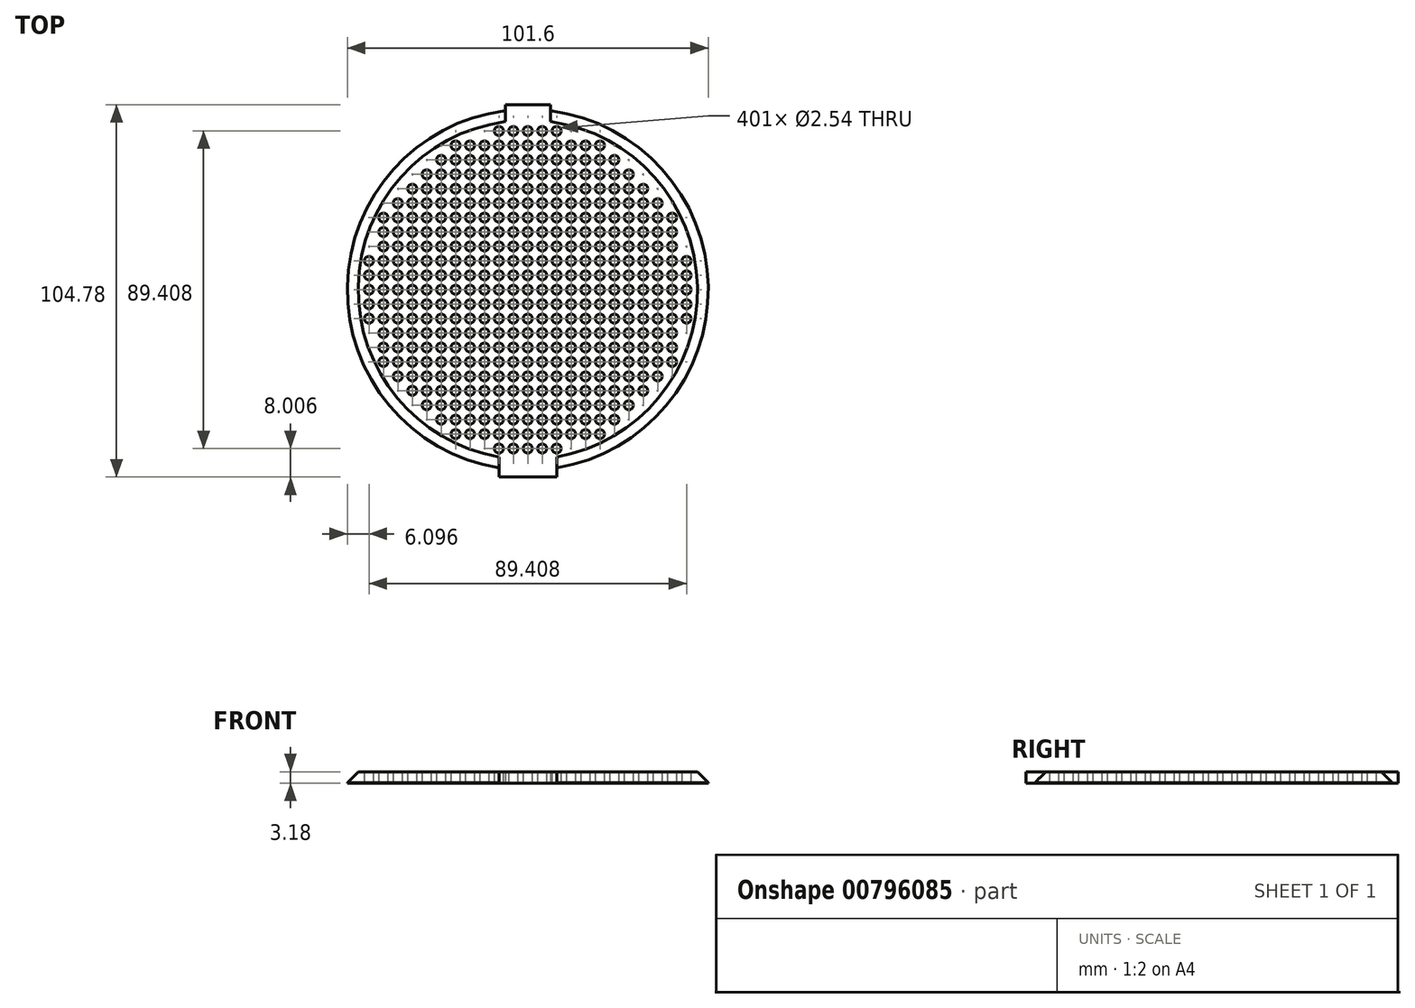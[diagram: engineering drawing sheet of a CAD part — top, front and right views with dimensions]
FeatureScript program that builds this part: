
annotation { "Feature Type Name" : "Feature", "Feature Type Description" : "" }
export const myFeature = defineFeature(function(context is Context, id is Id, definition is map)
    precondition{}
    {
        {
            var Q0;
            Q0=qCreatedBy(makeId("Top.planeOp"),FACE);
            var sketch = newSketch(context, id + "F0", { "sketchPlane" : qUnion([Q0])});
            skCircle(sketch, "E0", {"center": v(0, 0) * mm, "radius": 50.8 * mm});
            skSolve(sketch);
        }
        {
            var Q0;
            Q0 = qSketchRegion(id + "F0", true);
            extrude(context, id + "F1", {"entities" : qUnion([Q0]), "depth" : 3.17 * mm, "offsetDistance" : 25.4 * mm});
        }
        {
            var Q0;
            Q0=makeQuery(id+"F1.opExtrude","CAP_EDGE",EDGE,{"disambiguationData":[OSD([sQuery(id+"F0.wireOp",EDGE,"E0")])],"isStart":false});
            chamfer(context, id + "F2", {"entities" : qUnion([Q0]), "width" : 3.05 * mm, "tangentPropagation" : true});
        }
        {
            var Q0;
            Q0=makeQuery(id+"F1.opExtrude","CAP_FACE",FACE,{"disambiguationData":[OSD([sQuery(id+"F0.wireOp",EDGE,"E0")])],"isStart":false});
            var sketch = newSketch(context, id + "F3", { "sketchPlane" : qUnion([Q0])});
            skCircle(sketch, "E1", {"center": v(0, 0) * mm, "radius": 1.27 * mm});
            skCircle(sketch, "E2.0.1.0", {"center": v(0, 4.06) * mm, "radius": 1.27 * mm});
            skCircle(sketch, "E2.0.2.0", {"center": v(0, 8.13) * mm, "radius": 1.27 * mm});
            skCircle(sketch, "E2.0.3.0", {"center": v(0, 12.2) * mm, "radius": 1.27 * mm});
            skCircle(sketch, "E2.0.4.0", {"center": v(0, 16.26) * mm, "radius": 1.27 * mm});
            skCircle(sketch, "E2.0.5.0", {"center": v(0, 20.32) * mm, "radius": 1.27 * mm});
            skCircle(sketch, "E2.0.6.0", {"center": v(0, 24.38) * mm, "radius": 1.27 * mm});
            skCircle(sketch, "E2.0.7.0", {"center": v(0, 28.45) * mm, "radius": 1.27 * mm});
            skCircle(sketch, "E2.0.8.0", {"center": v(0, 32.51) * mm, "radius": 1.27 * mm});
            skCircle(sketch, "E2.0.9.0", {"center": v(0, 36.58) * mm, "radius": 1.27 * mm});
            skCircle(sketch, "E2.0.10.0", {"center": v(0, 40.64) * mm, "radius": 1.27 * mm});
            skCircle(sketch, "E2.0.11.0", {"center": v(0, 44.7) * mm, "radius": 1.27 * mm});
            skCircle(sketch, "E2.1.0.0", {"center": v(4.06, 0) * mm, "radius": 1.27 * mm});
            skCircle(sketch, "E2.1.1.0", {"center": v(4.06, 4.06) * mm, "radius": 1.27 * mm});
            skCircle(sketch, "E2.1.2.0", {"center": v(4.06, 8.13) * mm, "radius": 1.27 * mm});
            skCircle(sketch, "E2.1.3.0", {"center": v(4.06, 12.2) * mm, "radius": 1.27 * mm});
            skCircle(sketch, "E2.1.4.0", {"center": v(4.06, 16.26) * mm, "radius": 1.27 * mm});
            skCircle(sketch, "E2.1.5.0", {"center": v(4.06, 20.32) * mm, "radius": 1.27 * mm});
            skCircle(sketch, "E2.1.6.0", {"center": v(4.06, 24.38) * mm, "radius": 1.27 * mm});
            skCircle(sketch, "E2.1.7.0", {"center": v(4.06, 28.45) * mm, "radius": 1.27 * mm});
            skCircle(sketch, "E2.1.8.0", {"center": v(4.06, 32.51) * mm, "radius": 1.27 * mm});
            skCircle(sketch, "E2.1.9.0", {"center": v(4.06, 36.58) * mm, "radius": 1.27 * mm});
            skCircle(sketch, "E2.1.10.0", {"center": v(4.06, 40.64) * mm, "radius": 1.27 * mm});
            skCircle(sketch, "E2.1.11.0", {"center": v(4.06, 44.7) * mm, "radius": 1.27 * mm});
            skCircle(sketch, "E2.2.0.0", {"center": v(8.13, 0) * mm, "radius": 1.27 * mm});
            skCircle(sketch, "E2.2.1.0", {"center": v(8.13, 4.06) * mm, "radius": 1.27 * mm});
            skCircle(sketch, "E2.2.2.0", {"center": v(8.13, 8.13) * mm, "radius": 1.27 * mm});
            skCircle(sketch, "E2.2.3.0", {"center": v(8.13, 12.2) * mm, "radius": 1.27 * mm});
            skCircle(sketch, "E2.2.4.0", {"center": v(8.13, 16.26) * mm, "radius": 1.27 * mm});
            skCircle(sketch, "E2.2.5.0", {"center": v(8.13, 20.32) * mm, "radius": 1.27 * mm});
            skCircle(sketch, "E2.2.6.0", {"center": v(8.13, 24.38) * mm, "radius": 1.27 * mm});
            skCircle(sketch, "E2.2.7.0", {"center": v(8.13, 28.45) * mm, "radius": 1.27 * mm});
            skCircle(sketch, "E2.2.8.0", {"center": v(8.13, 32.51) * mm, "radius": 1.27 * mm});
            skCircle(sketch, "E2.2.9.0", {"center": v(8.13, 36.58) * mm, "radius": 1.27 * mm});
            skCircle(sketch, "E2.2.10.0", {"center": v(8.13, 40.64) * mm, "radius": 1.27 * mm});
            skCircle(sketch, "E2.2.11.0", {"center": v(8.13, 44.7) * mm, "radius": 1.27 * mm});
            skCircle(sketch, "E2.3.0.0", {"center": v(12.2, 0) * mm, "radius": 1.27 * mm});
            skCircle(sketch, "E2.3.1.0", {"center": v(12.2, 4.06) * mm, "radius": 1.27 * mm});
            skCircle(sketch, "E2.3.2.0", {"center": v(12.2, 8.13) * mm, "radius": 1.27 * mm});
            skCircle(sketch, "E2.3.3.0", {"center": v(12.2, 12.2) * mm, "radius": 1.27 * mm});
            skCircle(sketch, "E2.3.4.0", {"center": v(12.2, 16.26) * mm, "radius": 1.27 * mm});
            skCircle(sketch, "E2.3.5.0", {"center": v(12.2, 20.32) * mm, "radius": 1.27 * mm});
            skCircle(sketch, "E2.3.6.0", {"center": v(12.2, 24.38) * mm, "radius": 1.27 * mm});
            skCircle(sketch, "E2.3.7.0", {"center": v(12.2, 28.45) * mm, "radius": 1.27 * mm});
            skCircle(sketch, "E2.3.8.0", {"center": v(12.2, 32.51) * mm, "radius": 1.27 * mm});
            skCircle(sketch, "E2.3.9.0", {"center": v(12.2, 36.58) * mm, "radius": 1.27 * mm});
            skCircle(sketch, "E2.3.10.0", {"center": v(12.2, 40.64) * mm, "radius": 1.27 * mm});
            skCircle(sketch, "E2.4.0.0", {"center": v(16.26, 0) * mm, "radius": 1.27 * mm});
            skCircle(sketch, "E2.4.1.0", {"center": v(16.26, 4.06) * mm, "radius": 1.27 * mm});
            skCircle(sketch, "E2.4.2.0", {"center": v(16.26, 8.13) * mm, "radius": 1.27 * mm});
            skCircle(sketch, "E2.4.3.0", {"center": v(16.26, 12.2) * mm, "radius": 1.27 * mm});
            skCircle(sketch, "E2.4.4.0", {"center": v(16.26, 16.26) * mm, "radius": 1.27 * mm});
            skCircle(sketch, "E2.4.5.0", {"center": v(16.26, 20.32) * mm, "radius": 1.27 * mm});
            skCircle(sketch, "E2.4.6.0", {"center": v(16.26, 24.38) * mm, "radius": 1.27 * mm});
            skCircle(sketch, "E2.4.7.0", {"center": v(16.26, 28.45) * mm, "radius": 1.27 * mm});
            skCircle(sketch, "E2.4.8.0", {"center": v(16.26, 32.51) * mm, "radius": 1.27 * mm});
            skCircle(sketch, "E2.4.9.0", {"center": v(16.26, 36.58) * mm, "radius": 1.27 * mm});
            skCircle(sketch, "E2.4.10.0", {"center": v(16.26, 40.64) * mm, "radius": 1.27 * mm});
            skCircle(sketch, "E2.5.0.0", {"center": v(20.32, 0) * mm, "radius": 1.27 * mm});
            skCircle(sketch, "E2.5.1.0", {"center": v(20.32, 4.06) * mm, "radius": 1.27 * mm});
            skCircle(sketch, "E2.5.2.0", {"center": v(20.32, 8.13) * mm, "radius": 1.27 * mm});
            skCircle(sketch, "E2.5.3.0", {"center": v(20.32, 12.2) * mm, "radius": 1.27 * mm});
            skCircle(sketch, "E2.5.4.0", {"center": v(20.32, 16.26) * mm, "radius": 1.27 * mm});
            skCircle(sketch, "E2.5.5.0", {"center": v(20.32, 20.32) * mm, "radius": 1.27 * mm});
            skCircle(sketch, "E2.5.6.0", {"center": v(20.32, 24.38) * mm, "radius": 1.27 * mm});
            skCircle(sketch, "E2.5.7.0", {"center": v(20.32, 28.45) * mm, "radius": 1.27 * mm});
            skCircle(sketch, "E2.5.8.0", {"center": v(20.32, 32.51) * mm, "radius": 1.27 * mm});
            skCircle(sketch, "E2.5.9.0", {"center": v(20.32, 36.58) * mm, "radius": 1.27 * mm});
            skCircle(sketch, "E2.5.10.0", {"center": v(20.32, 40.64) * mm, "radius": 1.27 * mm});
            skCircle(sketch, "E2.6.0.0", {"center": v(24.38, 0) * mm, "radius": 1.27 * mm});
            skCircle(sketch, "E2.6.1.0", {"center": v(24.38, 4.06) * mm, "radius": 1.27 * mm});
            skCircle(sketch, "E2.6.2.0", {"center": v(24.38, 8.13) * mm, "radius": 1.27 * mm});
            skCircle(sketch, "E2.6.3.0", {"center": v(24.38, 12.2) * mm, "radius": 1.27 * mm});
            skCircle(sketch, "E2.6.4.0", {"center": v(24.38, 16.26) * mm, "radius": 1.27 * mm});
            skCircle(sketch, "E2.6.5.0", {"center": v(24.38, 20.32) * mm, "radius": 1.27 * mm});
            skCircle(sketch, "E2.6.6.0", {"center": v(24.38, 24.38) * mm, "radius": 1.27 * mm});
            skCircle(sketch, "E2.6.7.0", {"center": v(24.38, 28.45) * mm, "radius": 1.27 * mm});
            skCircle(sketch, "E2.6.8.0", {"center": v(24.38, 32.51) * mm, "radius": 1.27 * mm});
            skCircle(sketch, "E2.6.9.0", {"center": v(24.38, 36.58) * mm, "radius": 1.27 * mm});
            skCircle(sketch, "E2.7.0.0", {"center": v(28.45, 0) * mm, "radius": 1.27 * mm});
            skCircle(sketch, "E2.7.1.0", {"center": v(28.45, 4.06) * mm, "radius": 1.27 * mm});
            skCircle(sketch, "E2.7.2.0", {"center": v(28.45, 8.13) * mm, "radius": 1.27 * mm});
            skCircle(sketch, "E2.7.3.0", {"center": v(28.45, 12.2) * mm, "radius": 1.27 * mm});
            skCircle(sketch, "E2.7.4.0", {"center": v(28.45, 16.26) * mm, "radius": 1.27 * mm});
            skCircle(sketch, "E2.7.5.0", {"center": v(28.45, 20.32) * mm, "radius": 1.27 * mm});
            skCircle(sketch, "E2.7.6.0", {"center": v(28.45, 24.38) * mm, "radius": 1.27 * mm});
            skCircle(sketch, "E2.7.7.0", {"center": v(28.45, 28.45) * mm, "radius": 1.27 * mm});
            skCircle(sketch, "E2.7.8.0", {"center": v(28.45, 32.51) * mm, "radius": 1.27 * mm});
            skCircle(sketch, "E2.8.0.0", {"center": v(32.51, 0) * mm, "radius": 1.27 * mm});
            skCircle(sketch, "E2.8.1.0", {"center": v(32.51, 4.06) * mm, "radius": 1.27 * mm});
            skCircle(sketch, "E2.8.2.0", {"center": v(32.51, 8.13) * mm, "radius": 1.27 * mm});
            skCircle(sketch, "E2.8.3.0", {"center": v(32.51, 12.2) * mm, "radius": 1.27 * mm});
            skCircle(sketch, "E2.8.4.0", {"center": v(32.51, 16.26) * mm, "radius": 1.27 * mm});
            skCircle(sketch, "E2.8.5.0", {"center": v(32.51, 20.32) * mm, "radius": 1.27 * mm});
            skCircle(sketch, "E2.8.6.0", {"center": v(32.51, 24.38) * mm, "radius": 1.27 * mm});
            skCircle(sketch, "E2.8.7.0", {"center": v(32.51, 28.45) * mm, "radius": 1.27 * mm});
            skCircle(sketch, "E2.9.0.0", {"center": v(36.58, 0) * mm, "radius": 1.27 * mm});
            skCircle(sketch, "E2.9.1.0", {"center": v(36.58, 4.06) * mm, "radius": 1.27 * mm});
            skCircle(sketch, "E2.9.2.0", {"center": v(36.58, 8.13) * mm, "radius": 1.27 * mm});
            skCircle(sketch, "E2.9.3.0", {"center": v(36.58, 12.2) * mm, "radius": 1.27 * mm});
            skCircle(sketch, "E2.9.4.0", {"center": v(36.58, 16.26) * mm, "radius": 1.27 * mm});
            skCircle(sketch, "E2.9.5.0", {"center": v(36.58, 20.32) * mm, "radius": 1.27 * mm});
            skCircle(sketch, "E2.9.6.0", {"center": v(36.58, 24.38) * mm, "radius": 1.27 * mm});
            skCircle(sketch, "E2.10.0.0", {"center": v(40.64, 0) * mm, "radius": 1.27 * mm});
            skCircle(sketch, "E2.10.1.0", {"center": v(40.64, 4.06) * mm, "radius": 1.27 * mm});
            skCircle(sketch, "E2.10.2.0", {"center": v(40.64, 8.13) * mm, "radius": 1.27 * mm});
            skCircle(sketch, "E2.10.3.0", {"center": v(40.64, 12.2) * mm, "radius": 1.27 * mm});
            skCircle(sketch, "E2.10.4.0", {"center": v(40.64, 16.26) * mm, "radius": 1.27 * mm});
            skCircle(sketch, "E2.10.5.0", {"center": v(40.64, 20.32) * mm, "radius": 1.27 * mm});
            skCircle(sketch, "E2.11.0.0", {"center": v(44.7, 0) * mm, "radius": 1.27 * mm});
            skCircle(sketch, "E2.11.1.0", {"center": v(44.7, 4.06) * mm, "radius": 1.27 * mm});
            skCircle(sketch, "E2.11.2.0", {"center": v(44.7, 8.13) * mm, "radius": 1.27 * mm});
            skLineSegment(sketch, "E2.direction1", {"start": v(0, 0) * mm, "end": v(4.06, 0) * mm, "construction": true});
            skLineSegment(sketch, "E2.direction2", {"start": v(0, 0) * mm, "end": v(0, 4.06) * mm, "construction": true});
            skCircle(sketch, "E3.MirrorC", {"center": v(-4.06, 4.06) * mm, "radius": 1.27 * mm});
            skCircle(sketch, "E4.MirrorC", {"center": v(-28.45, 0) * mm, "radius": 1.27 * mm});
            skCircle(sketch, "E5.MirrorC", {"center": v(-8.13, 20.32) * mm, "radius": 1.27 * mm});
            skCircle(sketch, "E6.MirrorC", {"center": v(-16.26, 20.32) * mm, "radius": 1.27 * mm});
            skCircle(sketch, "E7.MirrorC", {"center": v(-32.51, 24.38) * mm, "radius": 1.27 * mm});
            skCircle(sketch, "E8.MirrorC", {"center": v(-44.7, 4.06) * mm, "radius": 1.27 * mm});
            skCircle(sketch, "E9.MirrorC", {"center": v(-12.2, 36.58) * mm, "radius": 1.27 * mm});
            skCircle(sketch, "E10.MirrorC", {"center": v(-12.2, 40.64) * mm, "radius": 1.27 * mm});
            skCircle(sketch, "E11.MirrorC", {"center": v(-24.38, 0) * mm, "radius": 1.27 * mm});
            skCircle(sketch, "E12.MirrorC", {"center": v(-20.32, 12.2) * mm, "radius": 1.27 * mm});
            skCircle(sketch, "E13.MirrorC", {"center": v(-28.45, 20.32) * mm, "radius": 1.27 * mm});
            skCircle(sketch, "E14.MirrorC", {"center": v(-24.38, 32.51) * mm, "radius": 1.27 * mm});
            skCircle(sketch, "E15.MirrorC", {"center": v(-4.06, 36.58) * mm, "radius": 1.27 * mm});
            skCircle(sketch, "E16.MirrorC", {"center": v(-40.64, 20.32) * mm, "radius": 1.27 * mm});
            skCircle(sketch, "E17.MirrorC", {"center": v(-24.38, 28.45) * mm, "radius": 1.27 * mm});
            skCircle(sketch, "E18.MirrorC", {"center": v(-8.13, 16.26) * mm, "radius": 1.27 * mm});
            skCircle(sketch, "E19.MirrorC", {"center": v(-32.51, 16.26) * mm, "radius": 1.27 * mm});
            skCircle(sketch, "E20.MirrorC", {"center": v(-20.32, 8.13) * mm, "radius": 1.27 * mm});
            skCircle(sketch, "E21.MirrorC", {"center": v(-32.51, 12.2) * mm, "radius": 1.27 * mm});
            skCircle(sketch, "E22.MirrorC", {"center": v(-24.38, 24.38) * mm, "radius": 1.27 * mm});
            skCircle(sketch, "E23.MirrorC", {"center": v(-44.7, 0) * mm, "radius": 1.27 * mm});
            skCircle(sketch, "E24.MirrorC", {"center": v(-12.2, 0) * mm, "radius": 1.27 * mm});
            skCircle(sketch, "E25.MirrorC", {"center": v(-20.32, 40.64) * mm, "radius": 1.27 * mm});
            skCircle(sketch, "E26.MirrorC", {"center": v(-4.06, 32.51) * mm, "radius": 1.27 * mm});
            skCircle(sketch, "E27.MirrorC", {"center": v(-40.64, 16.26) * mm, "radius": 1.27 * mm});
            skCircle(sketch, "E28.MirrorC", {"center": v(-8.13, 12.2) * mm, "radius": 1.27 * mm});
            skCircle(sketch, "E29.MirrorC", {"center": v(-12.2, 28.45) * mm, "radius": 1.27 * mm});
            skCircle(sketch, "E30.MirrorC", {"center": v(-20.32, 4.06) * mm, "radius": 1.27 * mm});
            skCircle(sketch, "E31.MirrorC", {"center": v(-4.06, 28.45) * mm, "radius": 1.27 * mm});
            skCircle(sketch, "E32.MirrorC", {"center": v(-32.51, 8.13) * mm, "radius": 1.27 * mm});
            skCircle(sketch, "E33.MirrorC", {"center": v(-8.13, 8.13) * mm, "radius": 1.27 * mm});
            skCircle(sketch, "E34.MirrorC", {"center": v(-12.2, 24.38) * mm, "radius": 1.27 * mm});
            skCircle(sketch, "E35.MirrorC", {"center": v(-4.06, 0) * mm, "radius": 1.27 * mm});
            skCircle(sketch, "E36.MirrorC", {"center": v(-8.13, 40.64) * mm, "radius": 1.27 * mm});
            skCircle(sketch, "E37.MirrorC", {"center": v(-4.06, 24.38) * mm, "radius": 1.27 * mm});
            skCircle(sketch, "E38.MirrorC", {"center": v(-36.58, 12.2) * mm, "radius": 1.27 * mm});
            skCircle(sketch, "E39.MirrorC", {"center": v(-8.13, 4.06) * mm, "radius": 1.27 * mm});
            skCircle(sketch, "E40.MirrorC", {"center": v(-16.26, 40.64) * mm, "radius": 1.27 * mm});
            skCircle(sketch, "E41.MirrorC", {"center": v(-8.13, 44.7) * mm, "radius": 1.27 * mm});
            skCircle(sketch, "E42.MirrorC", {"center": v(-16.26, 16.26) * mm, "radius": 1.27 * mm});
            skCircle(sketch, "E43.MirrorC", {"center": v(-20.32, 36.58) * mm, "radius": 1.27 * mm});
            skCircle(sketch, "E44.MirrorC", {"center": v(-28.45, 16.26) * mm, "radius": 1.27 * mm});
            skCircle(sketch, "E45.MirrorC", {"center": v(-16.26, 8.13) * mm, "radius": 1.27 * mm});
            skCircle(sketch, "E46.MirrorC", {"center": v(-8.13, 36.58) * mm, "radius": 1.27 * mm});
            skCircle(sketch, "E47.MirrorC", {"center": v(-20.32, 28.45) * mm, "radius": 1.27 * mm});
            skCircle(sketch, "E48.MirrorC", {"center": v(-28.45, 8.13) * mm, "radius": 1.27 * mm});
            skCircle(sketch, "E49.MirrorC", {"center": v(-4.06, 20.32) * mm, "radius": 1.27 * mm});
            skCircle(sketch, "E50.MirrorC", {"center": v(-40.64, 4.06) * mm, "radius": 1.27 * mm});
            skCircle(sketch, "E51.MirrorC", {"center": v(-24.38, 12.2) * mm, "radius": 1.27 * mm});
            skCircle(sketch, "E52.MirrorC", {"center": v(-24.38, 20.32) * mm, "radius": 1.27 * mm});
            skCircle(sketch, "E53.MirrorC", {"center": v(-40.64, 12.2) * mm, "radius": 1.27 * mm});
            skCircle(sketch, "E54.MirrorC", {"center": v(-32.51, 0) * mm, "radius": 1.27 * mm});
            skCircle(sketch, "E55.MirrorC", {"center": v(-12.2, 16.26) * mm, "radius": 1.27 * mm});
            skCircle(sketch, "E56.MirrorC", {"center": v(-16.26, 36.58) * mm, "radius": 1.27 * mm});
            skCircle(sketch, "E57.MirrorC", {"center": v(-24.38, 8.13) * mm, "radius": 1.27 * mm});
            skCircle(sketch, "E58.MirrorC", {"center": v(-20.32, 0) * mm, "radius": 1.27 * mm});
            skCircle(sketch, "E59.MirrorC", {"center": v(-28.45, 32.51) * mm, "radius": 1.27 * mm});
            skCircle(sketch, "E60.MirrorC", {"center": v(-40.64, 0) * mm, "radius": 1.27 * mm});
            skCircle(sketch, "E61.MirrorC", {"center": v(-4.06, 16.26) * mm, "radius": 1.27 * mm});
            skCircle(sketch, "E62.MirrorC", {"center": v(-4.06, 44.7) * mm, "radius": 1.27 * mm});
            skCircle(sketch, "E63.MirrorC", {"center": v(-12.2, 12.2) * mm, "radius": 1.27 * mm});
            skCircle(sketch, "E64.MirrorC", {"center": v(-16.26, 32.51) * mm, "radius": 1.27 * mm});
            skCircle(sketch, "E65.MirrorC", {"center": v(-36.58, 0) * mm, "radius": 1.27 * mm});
            skLineSegment(sketch, "E66.MirrorCS", {"start": v(0, 0) * mm, "end": v(-4.06, 0) * mm, "construction": true});
            skCircle(sketch, "E67.MirrorC", {"center": v(-8.13, 32.51) * mm, "radius": 1.27 * mm});
            skCircle(sketch, "E68.MirrorC", {"center": v(-16.26, 4.06) * mm, "radius": 1.27 * mm});
            skCircle(sketch, "E69.MirrorC", {"center": v(-20.32, 24.38) * mm, "radius": 1.27 * mm});
            skCircle(sketch, "E70.MirrorC", {"center": v(-28.45, 4.06) * mm, "radius": 1.27 * mm});
            skCircle(sketch, "E71.MirrorC", {"center": v(-32.51, 28.45) * mm, "radius": 1.27 * mm});
            skCircle(sketch, "E72.MirrorC", {"center": v(-16.26, 0) * mm, "radius": 1.27 * mm});
            skCircle(sketch, "E73.MirrorC", {"center": v(-24.38, 4.06) * mm, "radius": 1.27 * mm});
            skCircle(sketch, "E74.MirrorC", {"center": v(-16.26, 28.45) * mm, "radius": 1.27 * mm});
            skCircle(sketch, "E75.MirrorC", {"center": v(-28.45, 28.45) * mm, "radius": 1.27 * mm});
            skCircle(sketch, "E76.MirrorC", {"center": v(-4.06, 40.64) * mm, "radius": 1.27 * mm});
            skCircle(sketch, "E77.MirrorC", {"center": v(-36.58, 20.32) * mm, "radius": 1.27 * mm});
            skCircle(sketch, "E78.MirrorC", {"center": v(-36.58, 8.13) * mm, "radius": 1.27 * mm});
            skCircle(sketch, "E79.MirrorC", {"center": v(-12.2, 4.06) * mm, "radius": 1.27 * mm});
            skCircle(sketch, "E80.MirrorC", {"center": v(-8.13, 24.38) * mm, "radius": 1.27 * mm});
            skCircle(sketch, "E81.MirrorC", {"center": v(-16.26, 24.38) * mm, "radius": 1.27 * mm});
            skCircle(sketch, "E82.MirrorC", {"center": v(-20.32, 16.26) * mm, "radius": 1.27 * mm});
            skCircle(sketch, "E83.MirrorC", {"center": v(-24.38, 36.58) * mm, "radius": 1.27 * mm});
            skCircle(sketch, "E84.MirrorC", {"center": v(-28.45, 24.38) * mm, "radius": 1.27 * mm});
            skCircle(sketch, "E85.MirrorC", {"center": v(-16.26, 12.2) * mm, "radius": 1.27 * mm});
            skCircle(sketch, "E86.MirrorC", {"center": v(-12.2, 32.51) * mm, "radius": 1.27 * mm});
            skCircle(sketch, "E87.MirrorC", {"center": v(-20.32, 32.51) * mm, "radius": 1.27 * mm});
            skCircle(sketch, "E88.MirrorC", {"center": v(-4.06, 12.2) * mm, "radius": 1.27 * mm});
            skCircle(sketch, "E89.MirrorC", {"center": v(-28.45, 12.2) * mm, "radius": 1.27 * mm});
            skCircle(sketch, "E90.MirrorC", {"center": v(-4.06, 8.13) * mm, "radius": 1.27 * mm});
            skCircle(sketch, "E91.MirrorC", {"center": v(-24.38, 16.26) * mm, "radius": 1.27 * mm});
            skCircle(sketch, "E92.MirrorC", {"center": v(-32.51, 4.06) * mm, "radius": 1.27 * mm});
            skCircle(sketch, "E93.MirrorC", {"center": v(-40.64, 8.13) * mm, "radius": 1.27 * mm});
            skCircle(sketch, "E94.MirrorC", {"center": v(-12.2, 20.32) * mm, "radius": 1.27 * mm});
            skCircle(sketch, "E95.MirrorC", {"center": v(-8.13, 0) * mm, "radius": 1.27 * mm});
            skCircle(sketch, "E96.MirrorC", {"center": v(-36.58, 4.06) * mm, "radius": 1.27 * mm});
            skCircle(sketch, "E97.MirrorC", {"center": v(-36.58, 24.38) * mm, "radius": 1.27 * mm});
            skCircle(sketch, "E98.MirrorC", {"center": v(-44.7, 8.13) * mm, "radius": 1.27 * mm});
            skCircle(sketch, "E99.MirrorC", {"center": v(-8.13, 28.45) * mm, "radius": 1.27 * mm});
            skCircle(sketch, "E100.MirrorC", {"center": v(-12.2, 8.13) * mm, "radius": 1.27 * mm});
            skCircle(sketch, "E101.MirrorC", {"center": v(-20.32, 20.32) * mm, "radius": 1.27 * mm});
            skCircle(sketch, "E102.MirrorC", {"center": v(-36.58, 16.26) * mm, "radius": 1.27 * mm});
            skCircle(sketch, "E103.MirrorC", {"center": v(-32.51, 20.32) * mm, "radius": 1.27 * mm});
            skCircle(sketch, "E104.MirrorC", {"center": v(0, -44.7) * mm, "radius": 1.27 * mm});
            skCircle(sketch, "E105.MirrorC", {"center": v(0, -40.64) * mm, "radius": 1.27 * mm});
            skCircle(sketch, "E106.MirrorC", {"center": v(0, -32.51) * mm, "radius": 1.27 * mm});
            skCircle(sketch, "E107.MirrorC", {"center": v(4.06, -4.06) * mm, "radius": 1.27 * mm});
            skCircle(sketch, "E108.MirrorC", {"center": v(0, -12.2) * mm, "radius": 1.27 * mm});
            skCircle(sketch, "E109.MirrorC", {"center": v(0, -36.58) * mm, "radius": 1.27 * mm});
            skCircle(sketch, "E110.MirrorC", {"center": v(0, -24.38) * mm, "radius": 1.27 * mm});
            skCircle(sketch, "E111.MirrorC", {"center": v(0, -28.45) * mm, "radius": 1.27 * mm});
            skCircle(sketch, "E112.MirrorC", {"center": v(0, -20.32) * mm, "radius": 1.27 * mm});
            skCircle(sketch, "E113.MirrorC", {"center": v(0, -8.13) * mm, "radius": 1.27 * mm});
            skCircle(sketch, "E114.MirrorC", {"center": v(0, -16.26) * mm, "radius": 1.27 * mm});
            skLineSegment(sketch, "E115.MirrorCS", {"start": v(0, 0) * mm, "end": v(0, -4.06) * mm, "construction": true});
            skCircle(sketch, "E116.MirrorC", {"center": v(0, -4.06) * mm, "radius": 1.27 * mm});
            skCircle(sketch, "E117.MirrorC", {"center": v(-8.13, -36.58) * mm, "radius": 1.27 * mm});
            skCircle(sketch, "E118.MirrorC", {"center": v(-24.38, -4.06) * mm, "radius": 1.27 * mm});
            skCircle(sketch, "E119.MirrorC", {"center": v(-4.06, -12.2) * mm, "radius": 1.27 * mm});
            skCircle(sketch, "E120.MirrorC", {"center": v(36.58, -16.26) * mm, "radius": 1.27 * mm});
            skCircle(sketch, "E121.MirrorC", {"center": v(-8.13, -20.32) * mm, "radius": 1.27 * mm});
            skCircle(sketch, "E122.MirrorC", {"center": v(-32.51, -12.2) * mm, "radius": 1.27 * mm});
            skCircle(sketch, "E123.MirrorC", {"center": v(16.26, -20.32) * mm, "radius": 1.27 * mm});
            skCircle(sketch, "E124.MirrorC", {"center": v(20.32, -40.64) * mm, "radius": 1.27 * mm});
            skCircle(sketch, "E125.MirrorC", {"center": v(28.45, -20.32) * mm, "radius": 1.27 * mm});
            skCircle(sketch, "E126.MirrorC", {"center": v(4.06, -32.51) * mm, "radius": 1.27 * mm});
            skCircle(sketch, "E127.MirrorC", {"center": v(-16.26, -8.13) * mm, "radius": 1.27 * mm});
            skCircle(sketch, "E128.MirrorC", {"center": v(-20.32, -32.51) * mm, "radius": 1.27 * mm});
            skCircle(sketch, "E129.MirrorC", {"center": v(36.58, -12.2) * mm, "radius": 1.27 * mm});
            skCircle(sketch, "E130.MirrorC", {"center": v(-20.32, -8.13) * mm, "radius": 1.27 * mm});
            skCircle(sketch, "E131.MirrorC", {"center": v(8.13, -44.7) * mm, "radius": 1.27 * mm});
            skCircle(sketch, "E132.MirrorC", {"center": v(16.26, -16.26) * mm, "radius": 1.27 * mm});
            skCircle(sketch, "E133.MirrorC", {"center": v(20.32, -36.58) * mm, "radius": 1.27 * mm});
            skCircle(sketch, "E134.MirrorC", {"center": v(28.45, -16.26) * mm, "radius": 1.27 * mm});
            skCircle(sketch, "E135.MirrorC", {"center": v(4.06, -28.45) * mm, "radius": 1.27 * mm});
            skCircle(sketch, "E136.MirrorC", {"center": v(-32.51, -20.32) * mm, "radius": 1.27 * mm});
            skCircle(sketch, "E137.MirrorC", {"center": v(36.58, -8.13) * mm, "radius": 1.27 * mm});
            skCircle(sketch, "E138.MirrorC", {"center": v(-4.06, -4.06) * mm, "radius": 1.27 * mm});
            skCircle(sketch, "E139.MirrorC", {"center": v(-32.51, -16.26) * mm, "radius": 1.27 * mm});
            skCircle(sketch, "E140.MirrorC", {"center": v(8.13, -40.64) * mm, "radius": 1.27 * mm});
            skCircle(sketch, "E141.MirrorC", {"center": v(16.26, -12.2) * mm, "radius": 1.27 * mm});
            skCircle(sketch, "E142.MirrorC", {"center": v(20.32, -32.51) * mm, "radius": 1.27 * mm});
            skCircle(sketch, "E143.MirrorC", {"center": v(28.45, -12.2) * mm, "radius": 1.27 * mm});
            skCircle(sketch, "E144.MirrorC", {"center": v(4.06, -12.2) * mm, "radius": 1.27 * mm});
            skCircle(sketch, "E145.MirrorC", {"center": v(4.06, -8.13) * mm, "radius": 1.27 * mm});
            skCircle(sketch, "E146.MirrorC", {"center": v(4.06, -24.38) * mm, "radius": 1.27 * mm});
            skCircle(sketch, "E147.MirrorC", {"center": v(-36.58, -16.26) * mm, "radius": 1.27 * mm});
            skCircle(sketch, "E148.MirrorC", {"center": v(-28.45, -16.26) * mm, "radius": 1.27 * mm});
            skCircle(sketch, "E149.MirrorC", {"center": v(-28.45, -32.51) * mm, "radius": 1.27 * mm});
            skCircle(sketch, "E150.MirrorC", {"center": v(-32.51, -28.45) * mm, "radius": 1.27 * mm});
            skCircle(sketch, "E151.MirrorC", {"center": v(-12.2, -32.51) * mm, "radius": 1.27 * mm});
            skCircle(sketch, "E152.MirrorC", {"center": v(8.13, -36.58) * mm, "radius": 1.27 * mm});
            skCircle(sketch, "E153.MirrorC", {"center": v(16.26, -8.13) * mm, "radius": 1.27 * mm});
            skCircle(sketch, "E154.MirrorC", {"center": v(20.32, -28.45) * mm, "radius": 1.27 * mm});
            skCircle(sketch, "E155.MirrorC", {"center": v(28.45, -8.13) * mm, "radius": 1.27 * mm});
            skCircle(sketch, "E156.MirrorC", {"center": v(4.06, -20.32) * mm, "radius": 1.27 * mm});
            skCircle(sketch, "E157.MirrorC", {"center": v(-20.32, -20.32) * mm, "radius": 1.27 * mm});
            skCircle(sketch, "E158.MirrorC", {"center": v(-20.32, -36.58) * mm, "radius": 1.27 * mm});
            skCircle(sketch, "E159.MirrorC", {"center": v(-16.26, -12.2) * mm, "radius": 1.27 * mm});
            skCircle(sketch, "E160.MirrorC", {"center": v(36.58, -4.06) * mm, "radius": 1.27 * mm});
            skCircle(sketch, "E161.MirrorC", {"center": v(-8.13, -16.26) * mm, "radius": 1.27 * mm});
            skCircle(sketch, "E162.MirrorC", {"center": v(-4.06, -40.64) * mm, "radius": 1.27 * mm});
            skCircle(sketch, "E163.MirrorC", {"center": v(-12.2, -40.64) * mm, "radius": 1.27 * mm});
            skCircle(sketch, "E164.MirrorC", {"center": v(40.64, -8.13) * mm, "radius": 1.27 * mm});
            skCircle(sketch, "E165.MirrorC", {"center": v(8.13, -4.06) * mm, "radius": 1.27 * mm});
            skCircle(sketch, "E166.MirrorC", {"center": v(-40.64, -8.13) * mm, "radius": 1.27 * mm});
            skCircle(sketch, "E167.MirrorC", {"center": v(24.38, -16.26) * mm, "radius": 1.27 * mm});
            skCircle(sketch, "E168.MirrorC", {"center": v(-12.2, -12.2) * mm, "radius": 1.27 * mm});
            skCircle(sketch, "E169.MirrorC", {"center": v(-4.06, -32.51) * mm, "radius": 1.27 * mm});
            skCircle(sketch, "E170.MirrorC", {"center": v(12.2, -32.51) * mm, "radius": 1.27 * mm});
            skCircle(sketch, "E171.MirrorC", {"center": v(8.13, -16.26) * mm, "radius": 1.27 * mm});
            skCircle(sketch, "E172.MirrorC", {"center": v(-36.58, -20.32) * mm, "radius": 1.27 * mm});
            skCircle(sketch, "E173.MirrorC", {"center": v(12.2, -24.38) * mm, "radius": 1.27 * mm});
            skCircle(sketch, "E174.MirrorC", {"center": v(40.64, -20.32) * mm, "radius": 1.27 * mm});
            skCircle(sketch, "E175.MirrorC", {"center": v(32.51, -16.26) * mm, "radius": 1.27 * mm});
            skCircle(sketch, "E176.MirrorC", {"center": v(24.38, -28.45) * mm, "radius": 1.27 * mm});
            skCircle(sketch, "E177.MirrorC", {"center": v(24.38, -20.32) * mm, "radius": 1.27 * mm});
            skCircle(sketch, "E178.MirrorC", {"center": v(-36.58, -12.2) * mm, "radius": 1.27 * mm});
            skCircle(sketch, "E179.MirrorC", {"center": v(-36.58, -4.06) * mm, "radius": 1.27 * mm});
            skCircle(sketch, "E180.MirrorC", {"center": v(32.51, -8.13) * mm, "radius": 1.27 * mm});
            skCircle(sketch, "E181.MirrorC", {"center": v(8.13, -8.13) * mm, "radius": 1.27 * mm});
            skCircle(sketch, "E182.MirrorC", {"center": v(40.64, -12.2) * mm, "radius": 1.27 * mm});
            skCircle(sketch, "E183.MirrorC", {"center": v(-16.26, -32.51) * mm, "radius": 1.27 * mm});
            skCircle(sketch, "E184.MirrorC", {"center": v(-24.38, -20.32) * mm, "radius": 1.27 * mm});
            skCircle(sketch, "E185.MirrorC", {"center": v(-8.13, -40.64) * mm, "radius": 1.27 * mm});
            skCircle(sketch, "E186.MirrorC", {"center": v(-40.64, -16.26) * mm, "radius": 1.27 * mm});
            skCircle(sketch, "E187.MirrorC", {"center": v(-12.2, -20.32) * mm, "radius": 1.27 * mm});
            skCircle(sketch, "E188.MirrorC", {"center": v(-36.58, -8.13) * mm, "radius": 1.27 * mm});
            skCircle(sketch, "E189.MirrorC", {"center": v(12.2, -4.06) * mm, "radius": 1.27 * mm});
            skCircle(sketch, "E190.MirrorC", {"center": v(-24.38, -24.38) * mm, "radius": 1.27 * mm});
            skCircle(sketch, "E191.MirrorC", {"center": v(-16.26, -20.32) * mm, "radius": 1.27 * mm});
            skCircle(sketch, "E192.MirrorC", {"center": v(36.58, -20.32) * mm, "radius": 1.27 * mm});
            skCircle(sketch, "E193.MirrorC", {"center": v(-28.45, -12.2) * mm, "radius": 1.27 * mm});
            skCircle(sketch, "E194.MirrorC", {"center": v(28.45, -28.45) * mm, "radius": 1.27 * mm});
            skCircle(sketch, "E195.MirrorC", {"center": v(-32.51, -24.38) * mm, "radius": 1.27 * mm});
            skCircle(sketch, "E196.MirrorC", {"center": v(36.58, -24.38) * mm, "radius": 1.27 * mm});
            skCircle(sketch, "E197.MirrorC", {"center": v(-28.45, -8.13) * mm, "radius": 1.27 * mm});
            skCircle(sketch, "E198.MirrorC", {"center": v(16.26, -32.51) * mm, "radius": 1.27 * mm});
            skCircle(sketch, "E199.MirrorC", {"center": v(12.2, -12.2) * mm, "radius": 1.27 * mm});
            skCircle(sketch, "E200.MirrorC", {"center": v(20.32, -4.06) * mm, "radius": 1.27 * mm});
            skCircle(sketch, "E201.MirrorC", {"center": v(4.06, -36.58) * mm, "radius": 1.27 * mm});
            skCircle(sketch, "E202.MirrorC", {"center": v(8.13, -12.2) * mm, "radius": 1.27 * mm});
            skCircle(sketch, "E203.MirrorC", {"center": v(28.45, -24.38) * mm, "radius": 1.27 * mm});
            skCircle(sketch, "E204.MirrorC", {"center": v(24.38, -8.13) * mm, "radius": 1.27 * mm});
            skCircle(sketch, "E205.MirrorC", {"center": v(-4.06, -24.38) * mm, "radius": 1.27 * mm});
            skCircle(sketch, "E206.MirrorC", {"center": v(-40.64, -12.2) * mm, "radius": 1.27 * mm});
            skCircle(sketch, "E207.MirrorC", {"center": v(28.45, -32.51) * mm, "radius": 1.27 * mm});
            skCircle(sketch, "E208.MirrorC", {"center": v(-8.13, -12.2) * mm, "radius": 1.27 * mm});
            skCircle(sketch, "E209.MirrorC", {"center": v(-4.06, -20.32) * mm, "radius": 1.27 * mm});
            skCircle(sketch, "E210.MirrorC", {"center": v(24.38, -32.51) * mm, "radius": 1.27 * mm});
            skCircle(sketch, "E211.MirrorC", {"center": v(16.26, -24.38) * mm, "radius": 1.27 * mm});
            skCircle(sketch, "E212.MirrorC", {"center": v(20.32, -12.2) * mm, "radius": 1.27 * mm});
            skCircle(sketch, "E213.MirrorC", {"center": v(12.2, -36.58) * mm, "radius": 1.27 * mm});
            skCircle(sketch, "E214.MirrorC", {"center": v(-16.26, -28.45) * mm, "radius": 1.27 * mm});
            skCircle(sketch, "E215.MirrorC", {"center": v(8.13, -20.32) * mm, "radius": 1.27 * mm});
            skCircle(sketch, "E216.MirrorC", {"center": v(16.26, -36.58) * mm, "radius": 1.27 * mm});
            skCircle(sketch, "E217.MirrorC", {"center": v(-20.32, -28.45) * mm, "radius": 1.27 * mm});
            skCircle(sketch, "E218.MirrorC", {"center": v(12.2, -16.26) * mm, "radius": 1.27 * mm});
            skCircle(sketch, "E219.MirrorC", {"center": v(-20.32, -4.06) * mm, "radius": 1.27 * mm});
            skCircle(sketch, "E220.MirrorC", {"center": v(-24.38, -32.51) * mm, "radius": 1.27 * mm});
            skCircle(sketch, "E221.MirrorC", {"center": v(-12.2, -36.58) * mm, "radius": 1.27 * mm});
            skCircle(sketch, "E222.MirrorC", {"center": v(40.64, -4.06) * mm, "radius": 1.27 * mm});
            skCircle(sketch, "E223.MirrorC", {"center": v(24.38, -12.2) * mm, "radius": 1.27 * mm});
            skCircle(sketch, "E224.MirrorC", {"center": v(-16.26, -24.38) * mm, "radius": 1.27 * mm});
            skCircle(sketch, "E225.MirrorC", {"center": v(-8.13, -32.51) * mm, "radius": 1.27 * mm});
            skCircle(sketch, "E226.MirrorC", {"center": v(4.06, -40.64) * mm, "radius": 1.27 * mm});
            skCircle(sketch, "E227.MirrorC", {"center": v(-12.2, -16.26) * mm, "radius": 1.27 * mm});
            skCircle(sketch, "E228.MirrorC", {"center": v(-8.13, -4.06) * mm, "radius": 1.27 * mm});
            skCircle(sketch, "E229.MirrorC", {"center": v(-36.58, -24.38) * mm, "radius": 1.27 * mm});
            skCircle(sketch, "E230.MirrorC", {"center": v(24.38, -4.06) * mm, "radius": 1.27 * mm});
            skCircle(sketch, "E231.MirrorC", {"center": v(16.26, -28.45) * mm, "radius": 1.27 * mm});
            skCircle(sketch, "E232.MirrorC", {"center": v(12.2, -8.13) * mm, "radius": 1.27 * mm});
            skCircle(sketch, "E233.MirrorC", {"center": v(-4.06, -8.13) * mm, "radius": 1.27 * mm});
            skCircle(sketch, "E234.MirrorC", {"center": v(-28.45, -28.45) * mm, "radius": 1.27 * mm});
            skCircle(sketch, "E235.MirrorC", {"center": v(-4.06, -16.26) * mm, "radius": 1.27 * mm});
            skCircle(sketch, "E236.MirrorC", {"center": v(-4.06, -44.7) * mm, "radius": 1.27 * mm});
            skCircle(sketch, "E237.MirrorC", {"center": v(-20.32, -40.64) * mm, "radius": 1.27 * mm});
            skCircle(sketch, "E238.MirrorC", {"center": v(16.26, -40.64) * mm, "radius": 1.27 * mm});
            skCircle(sketch, "E239.MirrorC", {"center": v(12.2, -20.32) * mm, "radius": 1.27 * mm});
            skCircle(sketch, "E240.MirrorC", {"center": v(32.51, -4.06) * mm, "radius": 1.27 * mm});
            skCircle(sketch, "E241.MirrorC", {"center": v(-24.38, -12.2) * mm, "radius": 1.27 * mm});
            skCircle(sketch, "E242.MirrorC", {"center": v(20.32, -8.13) * mm, "radius": 1.27 * mm});
            skCircle(sketch, "E243.MirrorC", {"center": v(-28.45, -20.32) * mm, "radius": 1.27 * mm});
            skCircle(sketch, "E244.MirrorC", {"center": v(-12.2, -28.45) * mm, "radius": 1.27 * mm});
            skCircle(sketch, "E245.MirrorC", {"center": v(-8.13, -24.38) * mm, "radius": 1.27 * mm});
            skCircle(sketch, "E246.MirrorC", {"center": v(4.06, -44.7) * mm, "radius": 1.27 * mm});
            skCircle(sketch, "E247.MirrorC", {"center": v(24.38, -36.58) * mm, "radius": 1.27 * mm});
            skCircle(sketch, "E248.MirrorC", {"center": v(12.2, -40.64) * mm, "radius": 1.27 * mm});
            skCircle(sketch, "E249.MirrorC", {"center": v(8.13, -24.38) * mm, "radius": 1.27 * mm});
            skCircle(sketch, "E250.MirrorC", {"center": v(-4.06, -28.45) * mm, "radius": 1.27 * mm});
            skCircle(sketch, "E251.MirrorC", {"center": v(-4.06, -36.58) * mm, "radius": 1.27 * mm});
            skCircle(sketch, "E252.MirrorC", {"center": v(44.7, -4.06) * mm, "radius": 1.27 * mm});
            skCircle(sketch, "E253.MirrorC", {"center": v(32.51, -24.38) * mm, "radius": 1.27 * mm});
            skCircle(sketch, "E254.MirrorC", {"center": v(-20.32, -16.26) * mm, "radius": 1.27 * mm});
            skCircle(sketch, "E255.MirrorC", {"center": v(-16.26, -4.06) * mm, "radius": 1.27 * mm});
            skCircle(sketch, "E256.MirrorC", {"center": v(-16.26, -36.58) * mm, "radius": 1.27 * mm});
            skCircle(sketch, "E257.MirrorC", {"center": v(-16.26, -40.64) * mm, "radius": 1.27 * mm});
            skCircle(sketch, "E258.MirrorC", {"center": v(-44.7, -8.13) * mm, "radius": 1.27 * mm});
            skCircle(sketch, "E259.MirrorC", {"center": v(12.2, -28.45) * mm, "radius": 1.27 * mm});
            skCircle(sketch, "E260.MirrorC", {"center": v(-20.32, -12.2) * mm, "radius": 1.27 * mm});
            skCircle(sketch, "E261.MirrorC", {"center": v(40.64, -16.26) * mm, "radius": 1.27 * mm});
            skCircle(sketch, "E262.MirrorC", {"center": v(20.32, -20.32) * mm, "radius": 1.27 * mm});
            skCircle(sketch, "E263.MirrorC", {"center": v(32.51, -12.2) * mm, "radius": 1.27 * mm});
            skCircle(sketch, "E264.MirrorC", {"center": v(-44.7, -4.06) * mm, "radius": 1.27 * mm});
            skCircle(sketch, "E265.MirrorC", {"center": v(8.13, -28.45) * mm, "radius": 1.27 * mm});
            skCircle(sketch, "E266.MirrorC", {"center": v(-32.51, -8.13) * mm, "radius": 1.27 * mm});
            skCircle(sketch, "E267.MirrorC", {"center": v(-40.64, -20.32) * mm, "radius": 1.27 * mm});
            skCircle(sketch, "E268.MirrorC", {"center": v(24.38, -24.38) * mm, "radius": 1.27 * mm});
            skCircle(sketch, "E269.MirrorC", {"center": v(44.7, -8.13) * mm, "radius": 1.27 * mm});
            skCircle(sketch, "E270.MirrorC", {"center": v(32.51, -28.45) * mm, "radius": 1.27 * mm});
            skCircle(sketch, "E271.MirrorC", {"center": v(-24.38, -36.58) * mm, "radius": 1.27 * mm});
            skCircle(sketch, "E272.MirrorC", {"center": v(-24.38, -16.26) * mm, "radius": 1.27 * mm});
            skCircle(sketch, "E273.MirrorC", {"center": v(-20.32, -24.38) * mm, "radius": 1.27 * mm});
            skCircle(sketch, "E274.MirrorC", {"center": v(-8.13, -44.7) * mm, "radius": 1.27 * mm});
            skCircle(sketch, "E275.MirrorC", {"center": v(-12.2, -4.06) * mm, "radius": 1.27 * mm});
            skCircle(sketch, "E276.MirrorC", {"center": v(-8.13, -28.45) * mm, "radius": 1.27 * mm});
            skCircle(sketch, "E277.MirrorC", {"center": v(28.45, -4.06) * mm, "radius": 1.27 * mm});
            skCircle(sketch, "E278.MirrorC", {"center": v(20.32, -24.38) * mm, "radius": 1.27 * mm});
            skCircle(sketch, "E279.MirrorC", {"center": v(16.26, -4.06) * mm, "radius": 1.27 * mm});
            skCircle(sketch, "E280.MirrorC", {"center": v(8.13, -32.51) * mm, "radius": 1.27 * mm});
            skCircle(sketch, "E281.MirrorC", {"center": v(-8.13, -8.13) * mm, "radius": 1.27 * mm});
            skCircle(sketch, "E282.MirrorC", {"center": v(32.51, -20.32) * mm, "radius": 1.27 * mm});
            skCircle(sketch, "E283.MirrorC", {"center": v(-24.38, -28.45) * mm, "radius": 1.27 * mm});
            skCircle(sketch, "E284.MirrorC", {"center": v(-28.45, -24.38) * mm, "radius": 1.27 * mm});
            skCircle(sketch, "E285.MirrorC", {"center": v(-28.45, -4.06) * mm, "radius": 1.27 * mm});
            skCircle(sketch, "E286.MirrorC", {"center": v(-24.38, -8.13) * mm, "radius": 1.27 * mm});
            skCircle(sketch, "E287.MirrorC", {"center": v(-16.26, -16.26) * mm, "radius": 1.27 * mm});
            skCircle(sketch, "E288.MirrorC", {"center": v(-12.2, -8.13) * mm, "radius": 1.27 * mm});
            skCircle(sketch, "E289.MirrorC", {"center": v(-40.64, -4.06) * mm, "radius": 1.27 * mm});
            skCircle(sketch, "E290.MirrorC", {"center": v(-32.51, -4.06) * mm, "radius": 1.27 * mm});
            skCircle(sketch, "E291.MirrorC", {"center": v(4.06, -16.26) * mm, "radius": 1.27 * mm});
            skCircle(sketch, "E292.MirrorC", {"center": v(-12.2, -24.38) * mm, "radius": 1.27 * mm});
            skCircle(sketch, "E293.MirrorC", {"center": v(20.32, -16.26) * mm, "radius": 1.27 * mm});
            skSolve(sketch);
        }
        {
            var Q0;
            Q0 = qSketchRegion(id + "F3", true);
            extrude(context, id + "F4", {"entities" : qUnion([Q0]), "operationType" : NewBodyOperationType.REMOVE, "endBound" : BoundingType.THROUGH_ALL, "oppositeDirection" : true, "depth" : 25.4 * mm, "offsetDistance" : 25.4 * mm});
        }
        {
            var Q0;
            Q0=qCreatedBy(makeId("Front.planeOp"),FACE);
            cPlane(context, id + "F5", {"entities" : qUnion([Q0]), "cplaneType" : CPlaneType.OFFSET, "offset" : 50.8 * mm, "width" : 152.4 * mm, "height" : 152.4 * mm});
        }
        {
            var Q0;
            Q0=qCreatedBy(id+"F5.planeOp",FACE);
            var sketch = newSketch(context, id + "F6", { "sketchPlane" : qUnion([Q0])});
            skLineSegment(sketch, "E294.bottom", {"start": v(-8.13, 0) * mm, "end": v(8.13, 0) * mm});
            skLineSegment(sketch, "E294.top", {"start": v(-8.13, 3.18) * mm, "end": v(8.13, 3.18) * mm});
            skLineSegment(sketch, "E294.left", {"start": v(-8.13, 0) * mm, "end": v(-8.13, 3.18) * mm});
            skLineSegment(sketch, "E294.right", {"start": v(8.13, 0) * mm, "end": v(8.13, 3.18) * mm});
            skSolve(sketch);
        }
        {
            var Q0;
            Q0 = qSketchRegion(id + "F6", true);
            extrude(context, id + "F7", {"entities" : qUnion([Q0]), "operationType" : NewBodyOperationType.ADD, "depth" : 1.9 * mm, "offsetDistance" : 25.4 * mm, "hasSecondDirection" : true, "secondDirectionBound" : SecondDirectionBoundingType.UP_TO_NEXT, "secondDirectionOppositeDirection" : true, "secondDirectionDepth" : 25.4 * mm});
        }
        {
            var Q0;
            Q0=qCreatedBy(makeId("Front.planeOp"),FACE);
            cPlane(context, id + "F8", {"entities" : qUnion([Q0]), "cplaneType" : CPlaneType.OFFSET, "offset" : 50.8 * mm, "oppositeDirection" : true, "width" : 152.4 * mm, "height" : 152.4 * mm});
        }
        {
            var Q0;
            Q0=qCreatedBy(id+"F8.planeOp",FACE);
            var sketch = newSketch(context, id + "F9", { "sketchPlane" : qUnion([Q0])});
            skLineSegment(sketch, "E295", {"start": v(6.35, 3.18) * mm, "end": v(-6.35, 3.17) * mm});
            skLineSegment(sketch, "E296.top", {"start": v(6.35, 0) * mm, "end": v(-6.35, 0) * mm});
            skLineSegment(sketch, "E297", {"start": v(-6.35, 3.17) * mm, "end": v(-6.35, 0) * mm});
            skLineSegment(sketch, "E298", {"start": v(6.35, 3.18) * mm, "end": v(6.35, 0) * mm});
            skSolve(sketch);
        }
        {
            var Q0;
            Q0 = qSketchRegion(id + "F9", true);
            extrude(context, id + "F10", {"entities" : qUnion([Q0]), "operationType" : NewBodyOperationType.ADD, "depth" : 4.32 * mm, "offsetDistance" : 25.4 * mm, "hasSecondDirection" : true, "secondDirectionOppositeDirection" : true, "secondDirectionDepth" : 1.27 * mm});
        }
    });
